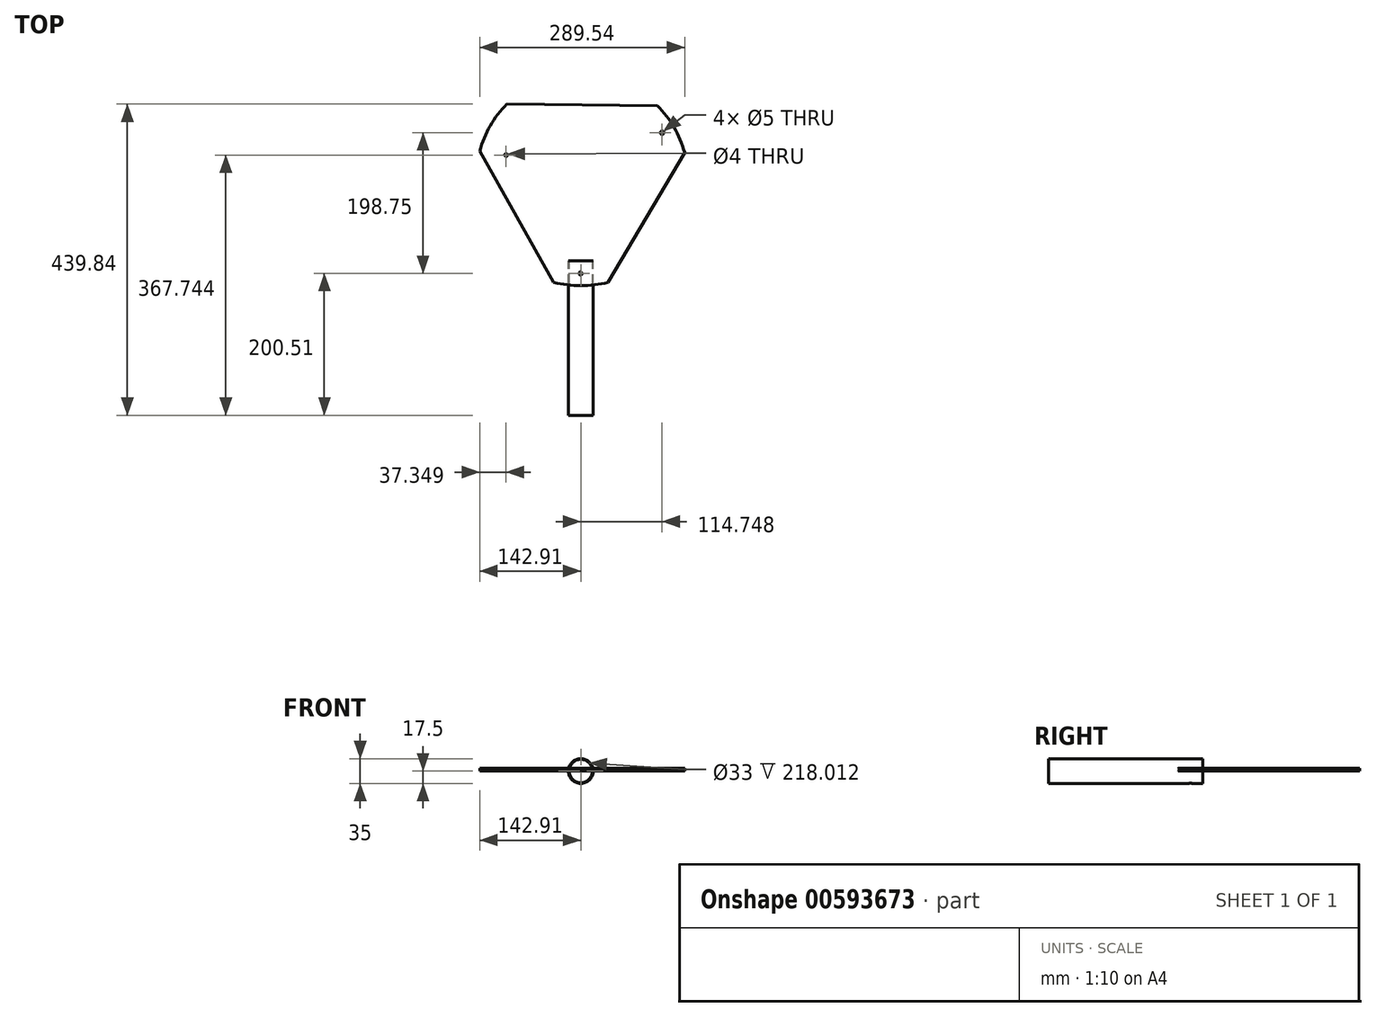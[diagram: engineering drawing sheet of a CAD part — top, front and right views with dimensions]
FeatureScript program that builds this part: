
annotation { "Feature Type Name" : "Feature", "Feature Type Description" : "" }
export const myFeature = defineFeature(function(context is Context, id is Id, definition is map)
    precondition{}
    {
        {
            var Q0;
            Q0=qCreatedBy(makeId("Top.planeOp"),FACE);
            var sketch = newSketch(context, id + "F0", { "sketchPlane" : qUnion([Q0])});
            skLineSegment(sketch, "E0", {"start": v(0, 0) * mm, "end": v(0, -364.15) * mm, "construction": true});
            skLineSegment(sketch, "E1", {"start": v(0, 0) * mm, "end": v(315.36, 182.07) * mm, "construction": true});
            skLineSegment(sketch, "E2", {"start": v(0, 0) * mm, "end": v(-315.36, 182.07) * mm, "construction": true});
            skCircle(sketch, "E3", {"center": v(-315.36, 182.07) * mm, "radius": 184.15 * mm, "construction": true});
            skCircle(sketch, "E4", {"center": v(315.36, 182.07) * mm, "radius": 184.15 * mm, "construction": true});
            skCircle(sketch, "E5", {"center": v(0, -364.15) * mm, "radius": 184.15 * mm, "construction": true});
            skCircle(sketch, "E6", {"center": v(0, 0) * mm, "radius": 150 * mm, "construction": true});
            skCircle(sketch, "E7", {"center": v(315.36, 182.07) * mm, "radius": 21 * mm, "construction": true});
            skCircle(sketch, "E8", {"center": v(0, -364.15) * mm, "radius": 21 * mm, "construction": true});
            skCircle(sketch, "E9", {"center": v(-315.36, 182.07) * mm, "radius": 21 * mm, "construction": true});
            skSolve(sketch);
        }
        {
            var Q0;
            Q0=qCreatedBy(makeId("Top.planeOp"),FACE);
            var sketch = newSketch(context, id + "F1", { "sketchPlane" : qUnion([Q0])});
            skLineSegment(sketch, "E10.bottom", {"start": v(-16.5, -115) * mm, "end": v(-16.5, -333.01) * mm});
            skLineSegment(sketch, "E10.top", {"start": v(-17.5, -115) * mm, "end": v(-17.5, -333.01) * mm});
            skLineSegment(sketch, "E10.left", {"start": v(-16.5, -115) * mm, "end": v(-17.5, -115) * mm});
            skLineSegment(sketch, "E10.right", {"start": v(-16.5, -333.01) * mm, "end": v(-17.5, -333.01) * mm});
            skLineSegment(sketch, "E11", {"start": v(-16.5, -333.01) * mm, "end": v(0, -333.01) * mm, "construction": true});
            skLineSegment(sketch, "E12", {"start": v(-16.5, -115) * mm, "end": v(0, -115) * mm, "construction": true});
            skSolve(sketch);
        }
        {
            var Q0;
            Q0=makeQuery(id+"F1.imprint","IMPRINT",FACE,{"disambiguationData":[TD([[makeQuery(id+"F1.imprint","IMPRINT",EDGE,{"derivedFrom":sQuery(id+"F1.wireOp",EDGE,"E10.bottom")}),-1.0]])]});
            var Q1;
            Q1=sQuery(id+"F0.wireOp",EDGE,"E0");
            revolve(context, id + "F2", {"entities" : qUnion([Q0]), "axis" : qUnion([Q1]), "revolveType" : RevolveType.FULL});
        }
        {
            var Q0;
            Q0=qCreatedBy(makeId("Top.planeOp"),FACE);
            var sketch = newSketch(context, id + "F3", { "sketchPlane" : qUnion([Q0])});
            skLineSegment(sketch, "E13", {"start": v(38.4, -145) * mm, "end": v(-38.4, -145) * mm, "construction": true});
            skPoint(sketch, "E14", {"position": v(0, -145) * mm});
            skArc(sketch, "E15", {"start": v(-38.4, -145) * mm, "mid": v(0, -149.88) * mm, "end": v(38.4, -145) * mm});
            skArc(sketch, "E16.1.0", {"start": v(146.63, 38.16) * mm, "mid": v(131.65, 73.86) * mm, "end": v(108.23, 104.68) * mm});
            skArc(sketch, "E16.2.0", {"start": v(-104.5, 106.83) * mm, "mid": v(-127.93, 76) * mm, "end": v(-142.91, 40.3) * mm});
            skPoint(sketch, "E16.center", {"position": v(1.24, 0) * mm});
            skLineSegment(sketch, "E17", {"start": v(-142.91, 40.3) * mm, "end": v(-38.4, -145) * mm});
            skLineSegment(sketch, "E18", {"start": v(38.4, -145) * mm, "end": v(146.63, 38.16) * mm});
            skLineSegment(sketch, "E19", {"start": v(-104.5, 106.83) * mm, "end": v(108.23, 104.68) * mm});
            skCircle(sketch, "E20", {"center": v(0, -132.5) * mm, "radius": 2.5 * mm});
            skCircle(sketch, "E21.1.0", {"center": v(114.75, 66.25) * mm, "radius": 2.5 * mm});
            skPoint(sketch, "E21.center", {"position": v(0, 0) * mm});
            skLineSegment(sketch, "E22", {"start": v(0, -149.88) * mm, "end": v(0, -132.5) * mm, "construction": true});
            skLineSegment(sketch, "E23", {"start": v(-105.56, 34.73) * mm, "end": v(-94.21, 54.4) * mm, "construction": true});
            skCircle(sketch, "E24", {"center": v(-105.56, 34.73) * mm, "radius": 2 * mm});
            skLineSegment(sketch, "E25", {"start": v(-94.21, 54.4) * mm, "end": v(-128.85, 74.4) * mm, "construction": true});
            skSolve(sketch);
        }
        {
            var Q0;
            Q0=makeQuery(id+"F3.imprint","IMPRINT",FACE,{"disambiguationData":[TD([[makeQuery(id+"F3.imprint","IMPRINT",EDGE,{"derivedFrom":sQuery(id+"F3.wireOp",EDGE,"E15")}),1.0]])]});
            extrude(context, id + "F4", {"entities" : qUnion([Q0]), "depth" : 4 * mm, "offsetDistance" : 25 * mm});
        }
        {
            var Q0;
            Q0=makeQuery(id+"F3.imprint","IMPRINT",FACE,{"disambiguationData":[TD([[makeQuery(id+"F3.imprint","IMPRINT",EDGE,{"derivedFrom":sQuery(id+"F3.wireOp",EDGE,"E20")}),1.0]])]});
            extrude(context, id + "F5", {"entities" : qUnion([Q0]), "operationType" : NewBodyOperationType.REMOVE, "endBound" : BoundingType.THROUGH_ALL, "oppositeDirection" : true, "depth" : 25 * mm, "offsetDistance" : 25 * mm, "hasSecondDirection" : true, "secondDirectionBound" : SecondDirectionBoundingType.THROUGH_ALL, "secondDirectionOppositeDirection" : false, "secondDirectionDepth" : 25 * mm});
        }
    });
